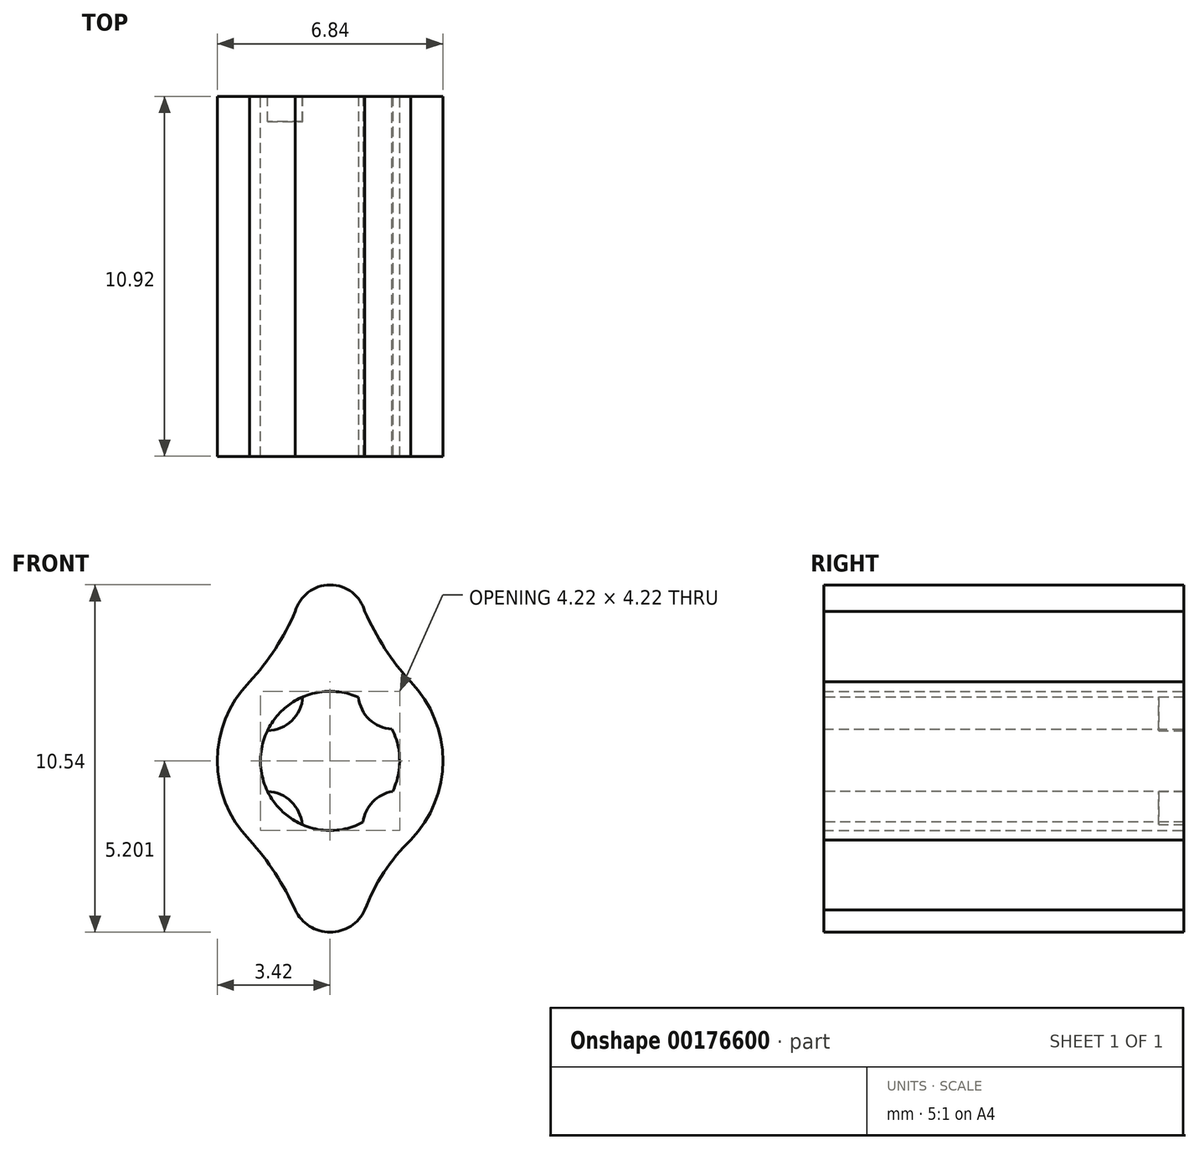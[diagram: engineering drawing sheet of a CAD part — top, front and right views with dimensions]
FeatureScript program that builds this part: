
annotation { "Feature Type Name" : "Feature", "Feature Type Description" : "" }
export const myFeature = defineFeature(function(context is Context, id is Id, definition is map)
    precondition{}
    {
        {
            var Q0;
            Q0=qCreatedBy(makeId("Front.planeOp"),FACE);
            var sketch = newSketch(context, id + "F0", { "sketchPlane" : qUnion([Q0])});
            skCircle(sketch, "E0", {"center": v(0, 0) * mm, "radius": 2.11 * mm});
            skLineSegment(sketch, "E1", {"start": v(0, 0) * mm, "end": v(0, 2.11) * mm});
            skLineSegment(sketch, "E2", {"start": v(0, 2.11) * mm, "end": v(0, 0) * mm});
            skLineSegment(sketch, "E3", {"start": v(0, 0) * mm, "end": v(0, -2.11) * mm});
            skLineSegment(sketch, "E4", {"start": v(0, 0) * mm, "end": v(-2.11, 0) * mm});
            skLineSegment(sketch, "E5", {"start": v(0, 0) * mm, "end": v(2.11, 0) * mm});
            skLineSegment(sketch, "E6", {"start": v(0, 0) * mm, "end": v(-1.52, 1.47) * mm});
            skLineSegment(sketch, "E7", {"start": v(0, 0) * mm, "end": v(1.52, 1.47) * mm});
            skLineSegment(sketch, "E8", {"start": v(0, 0) * mm, "end": v(1.52, -1.47) * mm});
            skLineSegment(sketch, "E9", {"start": v(0, 0) * mm, "end": v(-1.52, -1.47) * mm});
            skArc(sketch, "E10", {"start": v(-1.9, 0.91) * mm, "mid": v(-1.16, 1.22) * mm, "end": v(-0.83, 1.94) * mm});
            skArc(sketch, "E11", {"start": v(0.86, 1.93) * mm, "mid": v(1.2, 1.26) * mm, "end": v(1.88, 0.96) * mm});
            skArc(sketch, "E12", {"start": v(-0.85, -1.93) * mm, "mid": v(-1.18, -1.23) * mm, "end": v(-1.9, -0.93) * mm});
            skArc(sketch, "E13", {"start": v(1.9, -0.93) * mm, "mid": v(1.3, -1.25) * mm, "end": v(1, -1.86) * mm});
            skCircle(sketch, "E14", {"center": v(0, 0) * mm, "radius": 3.42 * mm});
            skLineSegment(sketch, "E15", {"start": v(-1.06, 0) * mm, "end": v(-1.06, 3.25) * mm});
            skLineSegment(sketch, "E16", {"start": v(1.06, 0) * mm, "end": v(1.06, 3.25) * mm});
            skLineSegment(sketch, "E17", {"start": v(-1.52, 1.47) * mm, "end": v(-2.44, 2.4) * mm});
            skLineSegment(sketch, "E18", {"start": v(1.52, 1.47) * mm, "end": v(2.44, 2.4) * mm});
            skLineSegment(sketch, "E19", {"start": v(1.52, -1.47) * mm, "end": v(2.44, -2.4) * mm});
            skLineSegment(sketch, "E20", {"start": v(-1.52, -1.47) * mm, "end": v(-2.44, -2.4) * mm});
            skLineSegment(sketch, "E21", {"start": v(-1.06, 0) * mm, "end": v(-1.06, -3.25) * mm});
            skLineSegment(sketch, "E22", {"start": v(1.06, -3.25) * mm, "end": v(1.06, 0) * mm});
            skLineSegment(sketch, "E23", {"start": v(-1.06, 3.25) * mm, "end": v(-1.06, 4.53) * mm});
            skLineSegment(sketch, "E24", {"start": v(1.06, 3.25) * mm, "end": v(1.06, 4.53) * mm});
            skLineSegment(sketch, "E25", {"start": v(-1.06, 4.53) * mm, "end": v(1.06, 4.53) * mm});
            skArc(sketch, "E26", {"start": v(-2.44, 2.4) * mm, "mid": v(-1.66, 3.4) * mm, "end": v(-1.06, 4.53) * mm});
            skArc(sketch, "E27", {"start": v(1.06, 4.53) * mm, "mid": v(1.66, 3.4) * mm, "end": v(2.44, 2.4) * mm});
            skArc(sketch, "E28", {"start": v(1.06, 4.53) * mm, "mid": v(0, 5.34) * mm, "end": v(-1.06, 4.53) * mm});
            skLineSegment(sketch, "E29", {"start": v(-1.06, -3.25) * mm, "end": v(-1.06, -4.53) * mm});
            skLineSegment(sketch, "E30", {"start": v(-1.06, -4.53) * mm, "end": v(1.06, -4.53) * mm});
            skLineSegment(sketch, "E31", {"start": v(1.06, -4.53) * mm, "end": v(1.06, -3.25) * mm});
            skArc(sketch, "E32", {"start": v(-1.06, -4.53) * mm, "mid": v(-1.67, -3.41) * mm, "end": v(-2.44, -2.4) * mm});
            skArc(sketch, "E33", {"start": v(2.44, -2.4) * mm, "mid": v(1.63, -3.38) * mm, "end": v(1.06, -4.53) * mm});
            skArc(sketch, "E34", {"start": v(-1.06, -4.53) * mm, "mid": v(0, -5.2) * mm, "end": v(1.06, -4.53) * mm});
            skSolve(sketch);
        }
        {
            var Q0;
            Q0=makeQuery(id+"F0.imprint","IMPRINT",FACE,{"disambiguationData":[TD([[makeQuery(id+"F0.imprint","IMPRINT",EDGE,{"derivedFrom":sQuery(id+"F0.wireOp",EDGE,"E25")}),1.0]])]});
            var Q1;
            {var subQ0=sQuery(id+"F0.wireOp",EDGE,"E23");Q1=makeQuery(id+"F0.imprint","IMPRINT",FACE,{"disambiguationData":[TD([[makeQuery(id+"F0.imprint","IMPRINT",EDGE,{"derivedFrom":subQ0}),-1.0]])]});}
            var Q2;
            {var subQ0=sQuery(id+"F0.wireOp",EDGE,"E24");Q2=makeQuery(id+"F0.imprint","IMPRINT",FACE,{"disambiguationData":[TD([[makeQuery(id+"F0.imprint","IMPRINT",EDGE,{"derivedFrom":subQ0}),-1.0]])]});}
            var Q3;
            {var subQ4=sQuery(id+"F0.wireOp",EDGE,"E18");Q3=makeQuery(id+"F0.imprint","IMPRINT",FACE,{"disambiguationData":[TD([[makeQuery(id+"F0.imprint","IMPRINT",EDGE,{"derivedFrom":subQ4}),-1.0]])]});}
            var Q4;
            {var subQ0=sQuery(id+"F0.wireOp",EDGE,"E0");var subQ7=makeQuery(id+"F0.imprint","INTERSECT",VERTEX,{"disambiguationData":[OD(0.0)],"derivedFrom":[subQ0,sQuery(id+"F0.wireOp",EDGE,"E11")]});Q4=makeQuery(id+"F0.imprint","IMPRINT",FACE,{"disambiguationData":[TD([[makeQuery(id+"F0.imprint","IMPRINT",EDGE,{"disambiguationData":[TD([[subQ7,1.0]])],"derivedFrom":subQ0}),-1.0]])]});}
            var Q5;
            {var subQ0=sQuery(id+"F0.wireOp",EDGE,"E17");Q5=makeQuery(id+"F0.imprint","IMPRINT",FACE,{"disambiguationData":[TD([[makeQuery(id+"F0.imprint","IMPRINT",EDGE,{"derivedFrom":subQ0}),-1.0]])]});}
            var Q6;
            {var subQ0=sQuery(id+"F0.wireOp",EDGE,"E18");Q6=makeQuery(id+"F0.imprint","IMPRINT",FACE,{"disambiguationData":[TD([[makeQuery(id+"F0.imprint","IMPRINT",EDGE,{"derivedFrom":subQ0}),1.0]])]});}
            var Q7;
            {var subQ0=sQuery(id+"F0.wireOp",EDGE,"E23");Q7=makeQuery(id+"F0.imprint","IMPRINT",FACE,{"disambiguationData":[TD([[makeQuery(id+"F0.imprint","IMPRINT",EDGE,{"derivedFrom":subQ0}),1.0]])]});}
            var Q8;
            {var subQ5=sQuery(id+"F0.wireOp",EDGE,"E17");Q8=makeQuery(id+"F0.imprint","IMPRINT",FACE,{"disambiguationData":[TD([[makeQuery(id+"F0.imprint","IMPRINT",EDGE,{"derivedFrom":subQ5}),1.0]])]});}
            var Q9;
            {var subQ0=sQuery(id+"F0.wireOp",EDGE,"E0");var subQ9=makeQuery(id+"F0.imprint","INTERSECT",VERTEX,{"disambiguationData":[OD(0.0)],"derivedFrom":[subQ0,sQuery(id+"F0.wireOp",EDGE,"E12")]});Q9=makeQuery(id+"F0.imprint","IMPRINT",FACE,{"disambiguationData":[TD([[makeQuery(id+"F0.imprint","IMPRINT",EDGE,{"disambiguationData":[TD([[subQ9,1.0]])],"derivedFrom":subQ0}),-1.0]])]});}
            var Q10;
            {var subQ5=sQuery(id+"F0.wireOp",EDGE,"E19");Q10=makeQuery(id+"F0.imprint","IMPRINT",FACE,{"disambiguationData":[TD([[makeQuery(id+"F0.imprint","IMPRINT",EDGE,{"derivedFrom":subQ5}),-1.0]])]});}
            var Q11;
            {var subQ0=sQuery(id+"F0.wireOp",EDGE,"E29");Q11=makeQuery(id+"F0.imprint","IMPRINT",FACE,{"disambiguationData":[TD([[makeQuery(id+"F0.imprint","IMPRINT",EDGE,{"derivedFrom":subQ0}),1.0]])]});}
            var Q12;
            {var subQ2=sQuery(id+"F0.wireOp",EDGE,"E29");Q12=makeQuery(id+"F0.imprint","IMPRINT",FACE,{"disambiguationData":[TD([[makeQuery(id+"F0.imprint","IMPRINT",EDGE,{"derivedFrom":subQ2}),-1.0]])]});}
            var Q13;
            {var subQ0=sQuery(id+"F0.wireOp",EDGE,"E20");Q13=makeQuery(id+"F0.imprint","IMPRINT",FACE,{"disambiguationData":[TD([[makeQuery(id+"F0.imprint","IMPRINT",EDGE,{"derivedFrom":subQ0}),1.0]])]});}
            var Q14;
            Q14=makeQuery(id+"F0.imprint","IMPRINT",FACE,{"disambiguationData":[TD([[makeQuery(id+"F0.imprint","IMPRINT",EDGE,{"derivedFrom":sQuery(id+"F0.wireOp",EDGE,"E30")}),-1.0]])]});
            var Q15;
            {var subQ0=sQuery(id+"F0.wireOp",EDGE,"E31");Q15=makeQuery(id+"F0.imprint","IMPRINT",FACE,{"disambiguationData":[TD([[makeQuery(id+"F0.imprint","IMPRINT",EDGE,{"derivedFrom":subQ0}),-1.0]])]});}
            var Q16;
            {var subQ1=sQuery(id+"F0.wireOp",EDGE,"E0");var subQ3=sQuery(id+"F0.wireOp",EDGE,"E13");var subQ4=makeQuery(id+"F0.imprint","INTERSECT",VERTEX,{"disambiguationData":[OD(0.0)],"derivedFrom":[subQ1,subQ3]});Q16=makeQuery(id+"F0.imprint","IMPRINT",FACE,{"disambiguationData":[TD([[makeQuery(id+"F0.imprint","IMPRINT",EDGE,{"disambiguationData":[TD([[subQ4,-1.0]])],"derivedFrom":subQ3}),1.0]])]});}
            var Q17;
            {var subQ0=sQuery(id+"F0.wireOp",EDGE,"E8");var subQ5=sQuery(id+"F0.wireOp",EDGE,"E13");var subQ6=makeQuery(id+"F0.imprint","INTERSECT",VERTEX,{"derivedFrom":[subQ0,subQ5]});Q17=makeQuery(id+"F0.imprint","IMPRINT",FACE,{"disambiguationData":[TD([[makeQuery(id+"F0.imprint","IMPRINT",EDGE,{"disambiguationData":[TD([[subQ6,-1.0]])],"derivedFrom":subQ5}),1.0]])]});}
            var Q18;
            {var subQ0=sQuery(id+"F0.wireOp",EDGE,"E13");var subQ1=sQuery(id+"F0.wireOp",EDGE,"E0");var subQ2=makeQuery(id+"F0.imprint","INTERSECT",VERTEX,{"disambiguationData":[OD(1.0)],"derivedFrom":[subQ1,subQ0]});Q18=makeQuery(id+"F0.imprint","IMPRINT",FACE,{"disambiguationData":[TD([[makeQuery(id+"F0.imprint","IMPRINT",EDGE,{"disambiguationData":[TD([[subQ2,-1.0]])],"derivedFrom":subQ1}),1.0]])]});}
            var Q19;
            {var subQ0=sQuery(id+"F0.wireOp",EDGE,"E12");var subQ1=sQuery(id+"F0.wireOp",EDGE,"E0");var subQ2=makeQuery(id+"F0.imprint","INTERSECT",VERTEX,{"disambiguationData":[OD(0.0)],"derivedFrom":[subQ1,subQ0]});Q19=makeQuery(id+"F0.imprint","IMPRINT",FACE,{"disambiguationData":[TD([[makeQuery(id+"F0.imprint","IMPRINT",EDGE,{"disambiguationData":[TD([[subQ2,1.0]])],"derivedFrom":subQ1}),1.0]])]});}
            var Q20;
            {var subQ0=sQuery(id+"F0.wireOp",EDGE,"E9");var subQ5=sQuery(id+"F0.wireOp",EDGE,"E12");var subQ6=makeQuery(id+"F0.imprint","INTERSECT",VERTEX,{"derivedFrom":[subQ0,subQ5]});Q20=makeQuery(id+"F0.imprint","IMPRINT",FACE,{"disambiguationData":[TD([[makeQuery(id+"F0.imprint","IMPRINT",EDGE,{"disambiguationData":[TD([[subQ6,1.0]])],"derivedFrom":subQ5}),1.0]])]});}
            var Q21;
            {var subQ1=sQuery(id+"F0.wireOp",EDGE,"E0");var subQ3=sQuery(id+"F0.wireOp",EDGE,"E12");var subQ4=makeQuery(id+"F0.imprint","INTERSECT",VERTEX,{"disambiguationData":[OD(1.0)],"derivedFrom":[subQ1,subQ3]});Q21=makeQuery(id+"F0.imprint","IMPRINT",FACE,{"disambiguationData":[TD([[makeQuery(id+"F0.imprint","IMPRINT",EDGE,{"disambiguationData":[TD([[subQ4,1.0]])],"derivedFrom":subQ3}),1.0]])]});}
            var Q22;
            {var subQ0=sQuery(id+"F0.wireOp",EDGE,"E10");var subQ1=sQuery(id+"F0.wireOp",EDGE,"E0");var subQ2=makeQuery(id+"F0.imprint","INTERSECT",VERTEX,{"disambiguationData":[OD(1.0)],"derivedFrom":[subQ1,subQ0]});Q22=makeQuery(id+"F0.imprint","IMPRINT",FACE,{"disambiguationData":[TD([[makeQuery(id+"F0.imprint","IMPRINT",EDGE,{"disambiguationData":[TD([[subQ2,-1.0]])],"derivedFrom":subQ1}),1.0]])]});}
            var Q23;
            {var subQ0=sQuery(id+"F0.wireOp",EDGE,"E6");var subQ5=sQuery(id+"F0.wireOp",EDGE,"E10");var subQ6=makeQuery(id+"F0.imprint","INTERSECT",VERTEX,{"derivedFrom":[subQ0,subQ5]});Q23=makeQuery(id+"F0.imprint","IMPRINT",FACE,{"disambiguationData":[TD([[makeQuery(id+"F0.imprint","IMPRINT",EDGE,{"disambiguationData":[TD([[subQ6,-1.0]])],"derivedFrom":subQ5}),1.0]])]});}
            var Q24;
            {var subQ1=sQuery(id+"F0.wireOp",EDGE,"E0");var subQ3=sQuery(id+"F0.wireOp",EDGE,"E10");var subQ4=makeQuery(id+"F0.imprint","INTERSECT",VERTEX,{"disambiguationData":[OD(0.0)],"derivedFrom":[subQ1,subQ3]});Q24=makeQuery(id+"F0.imprint","IMPRINT",FACE,{"disambiguationData":[TD([[makeQuery(id+"F0.imprint","IMPRINT",EDGE,{"disambiguationData":[TD([[subQ4,-1.0]])],"derivedFrom":subQ3}),1.0]])]});}
            var Q25;
            {var subQ0=sQuery(id+"F0.wireOp",EDGE,"E7");var subQ5=sQuery(id+"F0.wireOp",EDGE,"E11");var subQ6=makeQuery(id+"F0.imprint","INTERSECT",VERTEX,{"derivedFrom":[subQ0,subQ5]});Q25=makeQuery(id+"F0.imprint","IMPRINT",FACE,{"disambiguationData":[TD([[makeQuery(id+"F0.imprint","IMPRINT",EDGE,{"disambiguationData":[TD([[subQ6,1.0]])],"derivedFrom":subQ5}),1.0]])]});}
            var Q26;
            {var subQ1=sQuery(id+"F0.wireOp",EDGE,"E0");var subQ3=sQuery(id+"F0.wireOp",EDGE,"E11");var subQ4=makeQuery(id+"F0.imprint","INTERSECT",VERTEX,{"disambiguationData":[OD(1.0)],"derivedFrom":[subQ1,subQ3]});Q26=makeQuery(id+"F0.imprint","IMPRINT",FACE,{"disambiguationData":[TD([[makeQuery(id+"F0.imprint","IMPRINT",EDGE,{"disambiguationData":[TD([[subQ4,1.0]])],"derivedFrom":subQ3}),1.0]])]});}
            var Q27;
            {var subQ0=sQuery(id+"F0.wireOp",EDGE,"E11");var subQ1=sQuery(id+"F0.wireOp",EDGE,"E0");var subQ2=makeQuery(id+"F0.imprint","INTERSECT",VERTEX,{"disambiguationData":[OD(0.0)],"derivedFrom":[subQ1,subQ0]});Q27=makeQuery(id+"F0.imprint","IMPRINT",FACE,{"disambiguationData":[TD([[makeQuery(id+"F0.imprint","IMPRINT",EDGE,{"disambiguationData":[TD([[subQ2,1.0]])],"derivedFrom":subQ1}),1.0]])]});}
            extrude(context, id + "F1", {"entities" : qUnion([Q0, Q1, Q2, Q3, Q4, Q5, Q6, Q7, Q8, Q9, Q10, Q11, Q12, Q13, Q14, Q15, Q16, Q17, Q18, Q19, Q20, Q21, Q22, Q23, Q24, Q25, Q26, Q27]), "depth" : 10.92 * mm});
        }
        {
            var Q0;
            Q0=makeQuery(id+"F1.opExtrude","CAP_FACE",FACE,{"disambiguationData":[OSD([sQuery(id+"F0.wireOp",EDGE,"E0"),sQuery(id+"F0.wireOp",EDGE,"E10"),sQuery(id+"F0.wireOp",EDGE,"E11"),sQuery(id+"F0.wireOp",EDGE,"E12"),sQuery(id+"F0.wireOp",EDGE,"E13"),sQuery(id+"F0.wireOp",EDGE,"E14"),sQuery(id+"F0.wireOp",EDGE,"E26"),sQuery(id+"F0.wireOp",EDGE,"E27"),sQuery(id+"F0.wireOp",EDGE,"E28"),sQuery(id+"F0.wireOp",EDGE,"E32"),sQuery(id+"F0.wireOp",EDGE,"E33"),sQuery(id+"F0.wireOp",EDGE,"E34")])],"isStart":false});
            var sketch = newSketch(context, id + "F2", { "sketchPlane" : qUnion([Q0])});
            skCircle(sketch, "E35", {"center": v(0, 0) * mm, "radius": 2.11 * mm});
            skSolve(sketch);
        }
        {
            var Q0;
            {var subQ0=sQuery(id+"F2.wireOp",EDGE,"E35");var subQ1=makeQuery(id+"F1.opExtrude","CAP_EDGE",EDGE,{"disambiguationData":[OSD([sQuery(id+"F0.wireOp",EDGE,"E10")])],"isStart":false});var subQ2=makeQuery(id+"F2.imprint","INTERSECT",VERTEX,{"disambiguationData":[OD(0.0)],"derivedFrom":[subQ1,subQ0]});Q0=makeQuery(id+"F2.imprint","IMPRINT",FACE,{"disambiguationData":[TD([[makeQuery(id+"F2.imprint","IMPRINT",EDGE,{"disambiguationData":[TD([[subQ2,-1.0]])],"derivedFrom":subQ0}),1.0]])]});}
            var Q1;
            {var subQ0=sQuery(id+"F2.wireOp",EDGE,"E35");var subQ1=makeQuery(id+"F1.opExtrude","CAP_EDGE",EDGE,{"disambiguationData":[OSD([sQuery(id+"F0.wireOp",EDGE,"E11")])],"isStart":false});var subQ2=makeQuery(id+"F2.imprint","INTERSECT",VERTEX,{"disambiguationData":[OD(0.0)],"derivedFrom":[subQ1,subQ0]});Q1=makeQuery(id+"F2.imprint","IMPRINT",FACE,{"disambiguationData":[TD([[makeQuery(id+"F2.imprint","IMPRINT",EDGE,{"disambiguationData":[TD([[subQ2,1.0]])],"derivedFrom":subQ0}),1.0]])]});}
            var Q2;
            {var subQ0=sQuery(id+"F2.wireOp",EDGE,"E35");var subQ1=makeQuery(id+"F1.opExtrude","CAP_EDGE",EDGE,{"disambiguationData":[OSD([sQuery(id+"F0.wireOp",EDGE,"E13")])],"isStart":false});var subQ2=makeQuery(id+"F2.imprint","INTERSECT",VERTEX,{"disambiguationData":[OD(0.0)],"derivedFrom":[subQ1,subQ0]});Q2=makeQuery(id+"F2.imprint","IMPRINT",FACE,{"disambiguationData":[TD([[makeQuery(id+"F2.imprint","IMPRINT",EDGE,{"disambiguationData":[TD([[subQ2,-1.0]])],"derivedFrom":subQ0}),1.0]])]});}
            var Q3;
            {var subQ0=sQuery(id+"F2.wireOp",EDGE,"E35");var subQ1=makeQuery(id+"F1.opExtrude","CAP_EDGE",EDGE,{"disambiguationData":[OSD([sQuery(id+"F0.wireOp",EDGE,"E12")])],"isStart":false});var subQ2=makeQuery(id+"F2.imprint","INTERSECT",VERTEX,{"disambiguationData":[OD(0.0)],"derivedFrom":[subQ1,subQ0]});Q3=makeQuery(id+"F2.imprint","IMPRINT",FACE,{"disambiguationData":[TD([[makeQuery(id+"F2.imprint","IMPRINT",EDGE,{"disambiguationData":[TD([[subQ2,-1.0]])],"derivedFrom":subQ0}),1.0]])]});}
            extrude(context, id + "F3", {"entities" : qUnion([Q0, Q1, Q2, Q3]), "operationType" : NewBodyOperationType.REMOVE, "oppositeDirection" : true, "depth" : 10.16 * mm});
        }
    });
